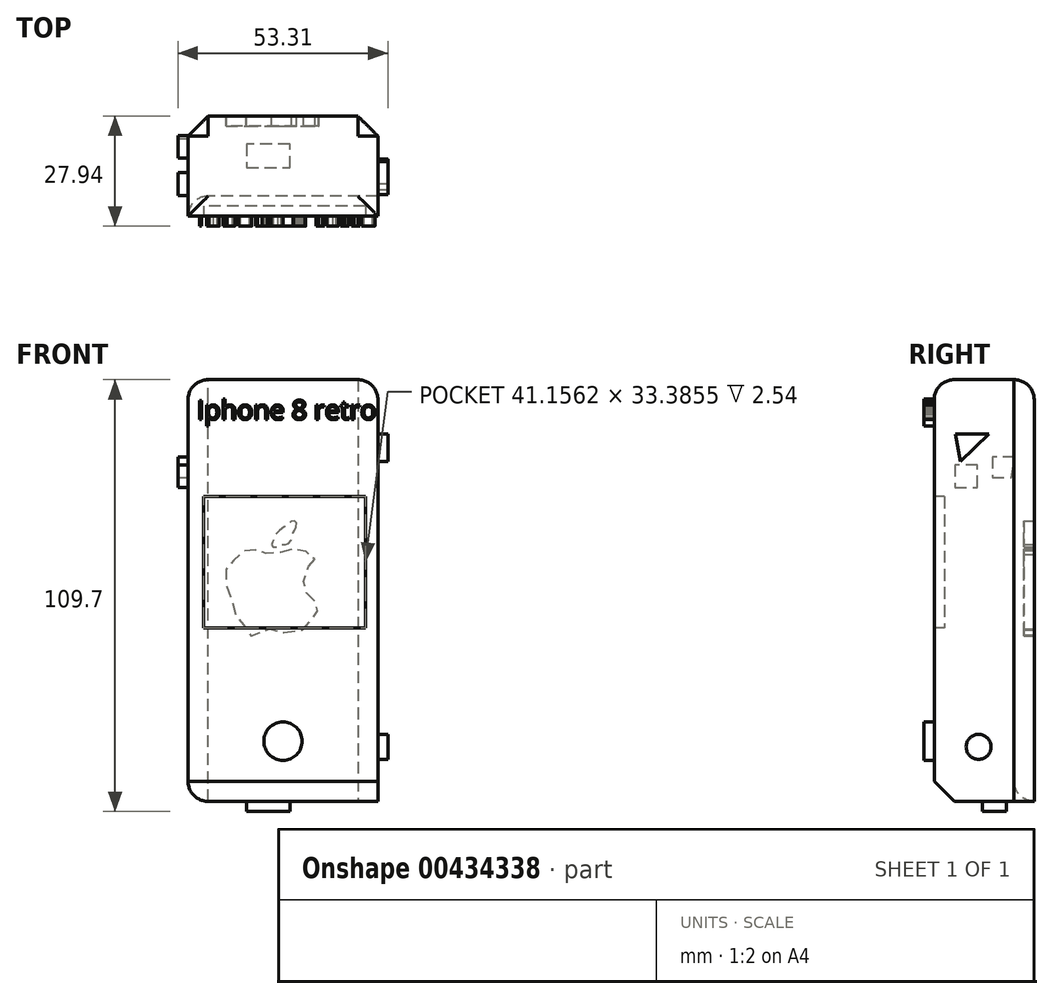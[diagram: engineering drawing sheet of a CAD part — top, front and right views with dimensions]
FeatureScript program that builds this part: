
annotation { "Feature Type Name" : "Feature", "Feature Type Description" : "" }
export const myFeature = defineFeature(function(context is Context, id is Id, definition is map)
    precondition{}
    {
        {
            var Q0;
            Q0=qCreatedBy(makeId("Front.planeOp"),FACE);
            var sketch = newSketch(context, id + "F0", { "sketchPlane" : qUnion([Q0])});
            skLineSegment(sketch, "E0", {"start": v(-14.86, -59.38) * mm, "end": v(-14.86, 50.42) * mm});
            skLineSegment(sketch, "E1", {"start": v(-14.86, 50.42) * mm, "end": v(33.37, 50.42) * mm});
            skLineSegment(sketch, "E2", {"start": v(33.37, -3.7) * mm, "end": v(33.37, 50.42) * mm});
            skLineSegment(sketch, "E3", {"start": v(33.37, -3.7) * mm, "end": v(33.37, -56.74) * mm});
            skLineSegment(sketch, "E4", {"start": v(33.37, -56.74) * mm, "end": v(-14.86, -56.74) * mm});
            skLineSegment(sketch, "E5", {"start": v(-14.86, -56.74) * mm, "end": v(-9.1, -56.74) * mm});
            skSolve(sketch);
        }
        {
            var Q0;
            {var subQ0=sQuery(id+"F0.wireOp",EDGE,"E1");Q0=makeQuery(id+"F0.imprint","IMPRINT",FACE,{"disambiguationData":[TD([[makeQuery(id+"F0.imprint","IMPRINT",EDGE,{"derivedFrom":subQ0}),-1.0]])]});}
            var sketch = newSketch(context, id + "F1", { "sketchPlane" : qUnion([Q0])});
            skLineSegment(sketch, "E6", {"start": v(-14.12, 49.55) * mm, "end": v(-38.3, 49.55) * mm});
            skLineSegment(sketch, "E7", {"start": v(-38.3, 49.55) * mm, "end": v(-38.3, -54.8) * mm});
            skLineSegment(sketch, "E8", {"start": v(-37.32, -54.8) * mm, "end": v(-15.16, -54.8) * mm});
            skLineSegment(sketch, "E9", {"start": v(33.95, 49.55) * mm, "end": v(56.68, 49.55) * mm});
            skLineSegment(sketch, "E10", {"start": v(56.68, 49.55) * mm, "end": v(56.68, -54.8) * mm});
            skLineSegment(sketch, "E11", {"start": v(56.68, -54.8) * mm, "end": v(33.48, -57.31) * mm});
            skSolve(sketch);
        }
        {
            var Q0;
            Q0 = qSketchRegion(id + "F0", true);
            extrude(context, id + "F2", {"entities" : qUnion([Q0]), "depth" : 25.4 * mm});
        }
        {
            var Q0;
            Q0=makeQuery(id+"F2.opExtrude","CAP_FACE",FACE,{"disambiguationData":[OSD([sQuery(id+"F0.wireOp",EDGE,"E0"),sQuery(id+"F0.wireOp",EDGE,"E1"),sQuery(id+"F0.wireOp",EDGE,"E2"),sQuery(id+"F0.wireOp",EDGE,"E3"),sQuery(id+"F0.wireOp",EDGE,"E4"),sQuery(id+"F0.wireOp",EDGE,"E5")])],"isStart":false});
            var sketch = newSketch(context, id + "F3", { "sketchPlane" : qUnion([Q0])});
            skCircle(sketch, "E12", {"center": v(9.25, -41.44) * mm, "radius": 4.87 * mm});
            skPoint(sketch, "E13", {"position": v(9.25, -56.74) * mm});
            skSolve(sketch);
        }
        {
            var Q0;
            Q0=makeQuery(id+"F3.imprint","IMPRINT",FACE,{"disambiguationData":[TD([[makeQuery(id+"F3.imprint","IMPRINT",EDGE,{"derivedFrom":sQuery(id+"F3.wireOp",EDGE,"E12")}),1.0]])]});
            extrude(context, id + "F4", {"entities" : qUnion([Q0]), "depth" : 2.54 * mm});
        }
        {
            var Q0;
            Q0=makeQuery(id+"F2.opExtrude","SWEPT_FACE",FACE,{"disambiguationData":[OSD([sQuery(id+"F0.wireOp",EDGE,"E2"),sQuery(id+"F0.wireOp",EDGE,"E3")])]});
            var sketch = newSketch(context, id + "F5", { "sketchPlane" : qUnion([Q0])});
            skCircle(sketch, "E14", {"center": v(-14.1, -42.88) * mm, "radius": 3.18 * mm});
            skSolve(sketch);
        }
        {
            var Q0;
            Q0=makeQuery(id+"F5.imprint","IMPRINT",FACE,{"disambiguationData":[TD([[makeQuery(id+"F5.imprint","IMPRINT",EDGE,{"derivedFrom":sQuery(id+"F5.wireOp",EDGE,"E14")}),1.0]])]});
            extrude(context, id + "F6", {"entities" : qUnion([Q0]), "depth" : 2.54 * mm});
        }
        {
            var Q0;
            Q0=makeQuery(id+"F2.opExtrude","SWEPT_FACE",FACE,{"disambiguationData":[OSD([sQuery(id+"F0.wireOp",EDGE,"E0")])]});
            var sketch = newSketch(context, id + "F7", { "sketchPlane" : qUnion([Q0])});
            skLineSegment(sketch, "E15", {"start": v(4.9, 30.8) * mm, "end": v(10.65, 30.8) * mm});
            skLineSegment(sketch, "E16", {"start": v(10.65, 30.8) * mm, "end": v(10.65, 25.61) * mm});
            skLineSegment(sketch, "E17", {"start": v(10.65, 25.61) * mm, "end": v(5.76, 25.61) * mm});
            skLineSegment(sketch, "E18", {"start": v(5.76, 25.61) * mm, "end": v(4.9, 30.8) * mm});
            skSolve(sketch);
        }
        {
            var Q0;
            Q0=makeQuery(id+"F7.imprint","IMPRINT",FACE,{"disambiguationData":[TD([[makeQuery(id+"F7.imprint","IMPRINT",EDGE,{"derivedFrom":sQuery(id+"F7.wireOp",EDGE,"E15")}),1.0]])]});
            var sketch = newSketch(context, id + "F8", { "sketchPlane" : qUnion([Q0])});
            skLineSegment(sketch, "E19", {"start": v(14.4, 28.78) * mm, "end": v(20.15, 28.78) * mm});
            skLineSegment(sketch, "E20", {"start": v(20.15, 28.78) * mm, "end": v(20.15, 23.02) * mm});
            skLineSegment(sketch, "E21", {"start": v(20.15, 23.02) * mm, "end": v(14.4, 23.02) * mm});
            skLineSegment(sketch, "E22", {"start": v(14.4, 23.02) * mm, "end": v(14.4, 28.78) * mm});
            skSolve(sketch);
        }
        {
            var Q0;
            Q0=makeQuery(id+"F7.imprint","IMPRINT",FACE,{"disambiguationData":[TD([[makeQuery(id+"F7.imprint","IMPRINT",EDGE,{"derivedFrom":sQuery(id+"F7.wireOp",EDGE,"E15")}),-1.0]])]});
            extrude(context, id + "F9", {"entities" : qUnion([Q0]), "depth" : 2.54 * mm});
        }
        {
            var Q0;
            Q0=makeQuery(id+"F8.imprint","IMPRINT",FACE,{"disambiguationData":[TD([[makeQuery(id+"F8.imprint","IMPRINT",EDGE,{"derivedFrom":sQuery(id+"F8.wireOp",EDGE,"E19")}),-1.0]])]});
            extrude(context, id + "F10", {"entities" : qUnion([Q0]), "operationType" : NewBodyOperationType.ADD, "depth" : 2.54 * mm});
        }
        {
            var Q0;
            Q0=makeQuery(id+"F2.opExtrude","CAP_FACE",FACE,{"disambiguationData":[OSD([sQuery(id+"F0.wireOp",EDGE,"E0"),sQuery(id+"F0.wireOp",EDGE,"E1"),sQuery(id+"F0.wireOp",EDGE,"E2"),sQuery(id+"F0.wireOp",EDGE,"E3"),sQuery(id+"F0.wireOp",EDGE,"E4"),sQuery(id+"F0.wireOp",EDGE,"E5")])],"isStart":false});
            var sketch = newSketch(context, id + "F11", { "sketchPlane" : qUnion([Q0])});
            skText(sketch, "E23", { "text": "Iphone 8 retro ", "fontName": "OpenSans-Regular.ttf"});
            const initialGuessF11  = {"E23": [-0.01266, 0.0403, 1, 0, 0.0049]};
            skSetInitialGuess(sketch, initialGuessF11);
            skSolve(sketch);
        }
        {
            var Q0;
            Q0 = qSketchRegion(id + "F11", true);
            extrude(context, id + "F12", {"entities" : qUnion([Q0]), "operationType" : NewBodyOperationType.ADD, "depth" : 2.54 * mm});
        }
        {
            var Q0;
            Q0=makeQuery(id+"F2.opExtrude","SWEPT_FACE",FACE,{"disambiguationData":[OSD([sQuery(id+"F0.wireOp",EDGE,"E2"),sQuery(id+"F0.wireOp",EDGE,"E3")])]});
            var sketch = newSketch(context, id + "F13", { "sketchPlane" : qUnion([Q0])});
            skLineSegment(sketch, "E24", {"start": v(-19.99, 36.56) * mm, "end": v(-10.52, 36.56) * mm});
            skLineSegment(sketch, "E25", {"start": v(-10.52, 37.53) * mm, "end": v(-18.73, 29.6) * mm});
            skLineSegment(sketch, "E26", {"start": v(-18.73, 29.6) * mm, "end": v(-19.99, 36.56) * mm});
            skSolve(sketch);
        }
        {
            var Q0;
            {var subQ0=sQuery(id+"F13.wireOp",EDGE,"E26");Q0=makeQuery(id+"F13.imprint","IMPRINT",FACE,{"disambiguationData":[TD([[makeQuery(id+"F13.imprint","IMPRINT",EDGE,{"derivedFrom":subQ0}),-1.0]])]});}
            extrude(context, id + "F14", {"entities" : qUnion([Q0]), "depth" : 2.54 * mm});
        }
        {
            var Q0;
            {var subQ0=sQuery(id+"F0.wireOp",EDGE,"E1");Q0=makeQuery(id+"F1.imprint","IMPRINT",FACE,{"disambiguationData":[TD([[makeQuery(id+"F1.imprint","IMPRINT",EDGE,{"derivedFrom":makeQuery(id+"F0.imprint","IMPRINT",EDGE,{"derivedFrom":subQ0})}),-1.0]])]});}
            var sketch = newSketch(context, id + "F15", { "sketchPlane" : qUnion([Q0])});
            skFitSpline(sketch, "E27", {"points": [v(15.75, 2.95) * mm, v(16.78, 4.07) * mm, v(17.34, 4.17) * mm, v(17.44, 4.54) * mm, v(17.06, 5.3) * mm, v(16.6, 5.48) * mm, v(15.37, 6.51) * mm, v(14.62, 6.89) * mm, v(13.87, 7.08) * mm, v(12.37, 7.36) * mm, v(11.34, 7.36) * mm, v(9.55, 6.89) * mm, v(7.77, 6.23) * mm, v(5.9, 6.04) * mm, v(4.68, 6.42) * mm, v(4.11, 6.8) * mm, v(3.83, 6.98) * mm, v(2.33, 7.08) * mm, v(2.05, 7.08) * mm, v(1.58, 7.26) * mm, v(0, 7.26) * mm, v(-1.61, 5.76) * mm, v(-2.83, 4.92) * mm, v(-3.4, 4.26) * mm, v(-3.96, 2.95) * mm, v(-5.1, 2.38) * mm, v(-5.1, 1.35) * mm, v(-5.1, 0) * mm, v(-5.1, -2.4) * mm, v(-3.96, -4.65) * mm, v(-3.58, -7.19) * mm, v(-3.3, -8.88) * mm, v(-2.64, -9.53) * mm, v(-1.99, -10.66) * mm, v(-1.42, -11.32) * mm, v(0, -12.82) * mm, v(0, -14.36) * mm, v(2.7, -14.36) * mm, v(5.43, -12.91) * mm, v(6.55, -13.1) * mm, v(8.9, -13.29) * mm, v(10.21, -14.36) * mm, v(13.78, -13.38) * mm, v(14.9, -12.54) * mm, v(15.28, -11.78) * mm, v(16.22, -10.94) * mm, v(16.6, -10.1) * mm, v(17.16, -9.06) * mm, v(18.3, -8.13) * mm, v(18.3, -7.37) * mm, v(18.3, -6.34) * mm, v(16.69, -5.87) * mm, v(15.84, -4.84) * mm, v(15.28, -3.9) * mm, v(15.1, -2.68) * mm, v(14.53, -1.46) * mm, v(14.53, -0.71) * mm, v(14.9, 0.88) * mm, v(15.75, 2.95) * mm]});
            skFitSpline(sketch, "E28", {"points": [v(12.56, 12.99) * mm, v(12.56, 14.36) * mm, v(11.34, 14.36) * mm, v(10.02, 13.36) * mm, v(7.87, 11.58) * mm, v(7.5, 11.2) * mm, v(7.02, 10.08) * mm, v(6.36, 8.67) * mm, v(6.46, 8.01) * mm, v(7.58, 7.92) * mm, v(8.15, 8.39) * mm, v(9.55, 8.58) * mm, v(10.68, 8.76) * mm, v(11.43, 9.9) * mm, v(11.43, 10.45) * mm, v(11.62, 11.11) * mm, v(12, 11.67) * mm, v(12.56, 12.99) * mm]});
            skSolve(sketch);
        }
        {
            var Q0;
            Q0 = qSketchRegion(id + "F15", true);
            extrude(context, id + "F16", {"entities" : qUnion([Q0]), "depth" : 2.54 * mm});
        }
        {
            var Q0;
            Q0=makeQuery(id+"F2.opExtrude","SWEPT_FACE",FACE,{"disambiguationData":[OSD([sQuery(id+"F0.wireOp",EDGE,"E4"),sQuery(id+"F0.wireOp",EDGE,"E5")])]});
            var sketch = newSketch(context, id + "F17", { "sketchPlane" : qUnion([Q0])});
            skLineSegment(sketch, "E29", {"start": v(0, 13.1) * mm, "end": v(11.05, 13.1) * mm});
            skLineSegment(sketch, "E30", {"start": v(11.05, 13.1) * mm, "end": v(11.05, 7.1) * mm});
            skLineSegment(sketch, "E31", {"start": v(11.05, 7.1) * mm, "end": v(0, 7.1) * mm});
            skLineSegment(sketch, "E32", {"start": v(0, 7.1) * mm, "end": v(0, 13.1) * mm});
            skSolve(sketch);
        }
        {
            var Q0;
            Q0 = qSketchRegion(id + "F17", true);
            extrude(context, id + "F18", {"entities" : qUnion([Q0]), "operationType" : NewBodyOperationType.ADD, "depth" : 2.54 * mm});
        }
        {
            var Q0;
            {var subQ0=sQuery(id+"F0.wireOp",EDGE,"E5");var subQ1=sQuery(id+"F0.wireOp",EDGE,"E4");var subQ2=sQuery(id+"F0.wireOp",EDGE,"E3");var subQ3=sQuery(id+"F0.wireOp",EDGE,"E2");var subQ4=sQuery(id+"F0.wireOp",EDGE,"E1");var subQ5=sQuery(id+"F0.wireOp",EDGE,"E0");Q0=makeQuery(id+"F12.boolean.opBoolean","SPLIT",FACE,{"disambiguationData":[TD([makeQuery(id+"F2.opExtrude","SWEPT_FACE",FACE,{"disambiguationData":[OSD([subQ5])]})])],"derivedFrom":makeQuery(id+"F2.opExtrude","CAP_FACE",FACE,{"disambiguationData":[OSD([subQ5,subQ4,subQ3,subQ2,subQ1,subQ0])],"isStart":false})});}
            var sketch = newSketch(context, id + "F19", { "sketchPlane" : qUnion([Q0])});
            skLineSegment(sketch, "E33", {"start": v(-10.94, 21.59) * mm, "end": v(-10.94, -12.66) * mm});
            skLineSegment(sketch, "E34", {"start": v(-10.94, -12.66) * mm, "end": v(30.22, -12.66) * mm});
            skLineSegment(sketch, "E35", {"start": v(30.22, -12.66) * mm, "end": v(30.22, 20.72) * mm});
            skLineSegment(sketch, "E36", {"start": v(30.22, 20.72) * mm, "end": v(-10.94, 20.72) * mm});
            skSolve(sketch);
        }
        {
            var Q0;
            Q0 = qSketchRegion(id + "F19", true);
            var Q1;
            Q1 = qConstructionFilter(qBodyType(qCreatedBy(id + "F19" ,EDGE), BodyType.WIRE), ConstructionObject.NO);
            extrude(context, id + "F20", {"entities" : qUnion([Q0]), "operationType" : NewBodyOperationType.REMOVE, "surfaceEntities" : qUnion([Q1]), "oppositeDirection" : true, "depth" : 2.54 * mm});
        }
        {
            var Q0;
            Q0=makeQuery(id+"F20.boolean.opBoolean","COPY",FACE,{"derivedFrom":makeQuery(id+"F20.opExtrude","CAP_FACE",FACE,{"disambiguationData":[OSD([sQuery(id+"F19.wireOp",EDGE,"E33"),sQuery(id+"F19.wireOp",EDGE,"E34"),sQuery(id+"F19.wireOp",EDGE,"E35"),sQuery(id+"F19.wireOp",EDGE,"E36")])],"isStart":false})});
            var sketch = newSketch(context, id + "F21", { "sketchPlane" : qUnion([Q0])});
            skLineSegment(sketch, "E37.bottom", {"start": v(-10.94, 20.72) * mm, "end": v(30.22, 20.72) * mm});
            skLineSegment(sketch, "E37.top", {"start": v(-10.94, -12.66) * mm, "end": v(30.22, -12.66) * mm});
            skLineSegment(sketch, "E37.left", {"start": v(-10.94, 20.72) * mm, "end": v(-10.94, -12.66) * mm});
            skLineSegment(sketch, "E37.right", {"start": v(30.22, 20.72) * mm, "end": v(30.22, -12.66) * mm});
            skSolve(sketch);
        }
        {
            var Q0;
            Q0 = qSketchRegion(id + "F21", true);
            extrude(context, id + "F22", {"entities" : qUnion([Q0]), "depth" : 2.54 * mm});
        }
        {
            var Q0;
            Q0=makeQuery(id+"F2.opExtrude","SWEPT_FACE",FACE,{"disambiguationData":[OSD([sQuery(id+"F0.wireOp",EDGE,"E1")])]});
            fillet(context, id + "F23", {"entities" : qUnion([Q0]), "radius" : 5.08 * mm, "tangentPropagation" : true, "allowEdgeOverflow" : false});
        }
        {
            var Q0;
            Q0=makeQuery(id+"F2.opExtrude","CAP_EDGE",EDGE,{"disambiguationData":[OSD([sQuery(id+"F0.wireOp",EDGE,"E2"),sQuery(id+"F0.wireOp",EDGE,"E3")])],"isStart":true});
            chamfer(context, id + "F24", {"entities" : qUnion([Q0]), "width" : 5.08 * mm, "tangentPropagation" : true});
        }
        {
            var Q0;
            Q0=makeQuery(id+"F2.opExtrude","CAP_EDGE",EDGE,{"disambiguationData":[OSD([sQuery(id+"F0.wireOp",EDGE,"E0")])],"isStart":true});
            chamfer(context, id + "F25", {"entities" : qUnion([Q0]), "width" : 5.08 * mm, "tangentPropagation" : true});
        }
        {
            var Q0;
            Q0=makeQuery(id+"F2.opExtrude","CAP_EDGE",EDGE,{"disambiguationData":[OSD([sQuery(id+"F0.wireOp",EDGE,"E4"),sQuery(id+"F0.wireOp",EDGE,"E5")])],"isStart":false});
            chamfer(context, id + "F26", {"entities" : qUnion([Q0]), "width" : 5.08 * mm, "tangentPropagation" : true});
        }
        {
            var Q0;
            Q0=makeQuery(id+"F2.opExtrude","SWEPT_EDGE",EDGE,{"disambiguationData":[OSD([sQuery(id+"F0.wireOp",EDGE,"E0"),sQuery(id+"F0.wireOp",EDGE,"E5")])]});
            fillet(context, id + "F27", {"entities" : qUnion([Q0]), "radius" : 5.08 * mm, "tangentPropagation" : true, "allowEdgeOverflow" : false});
        }
    });
